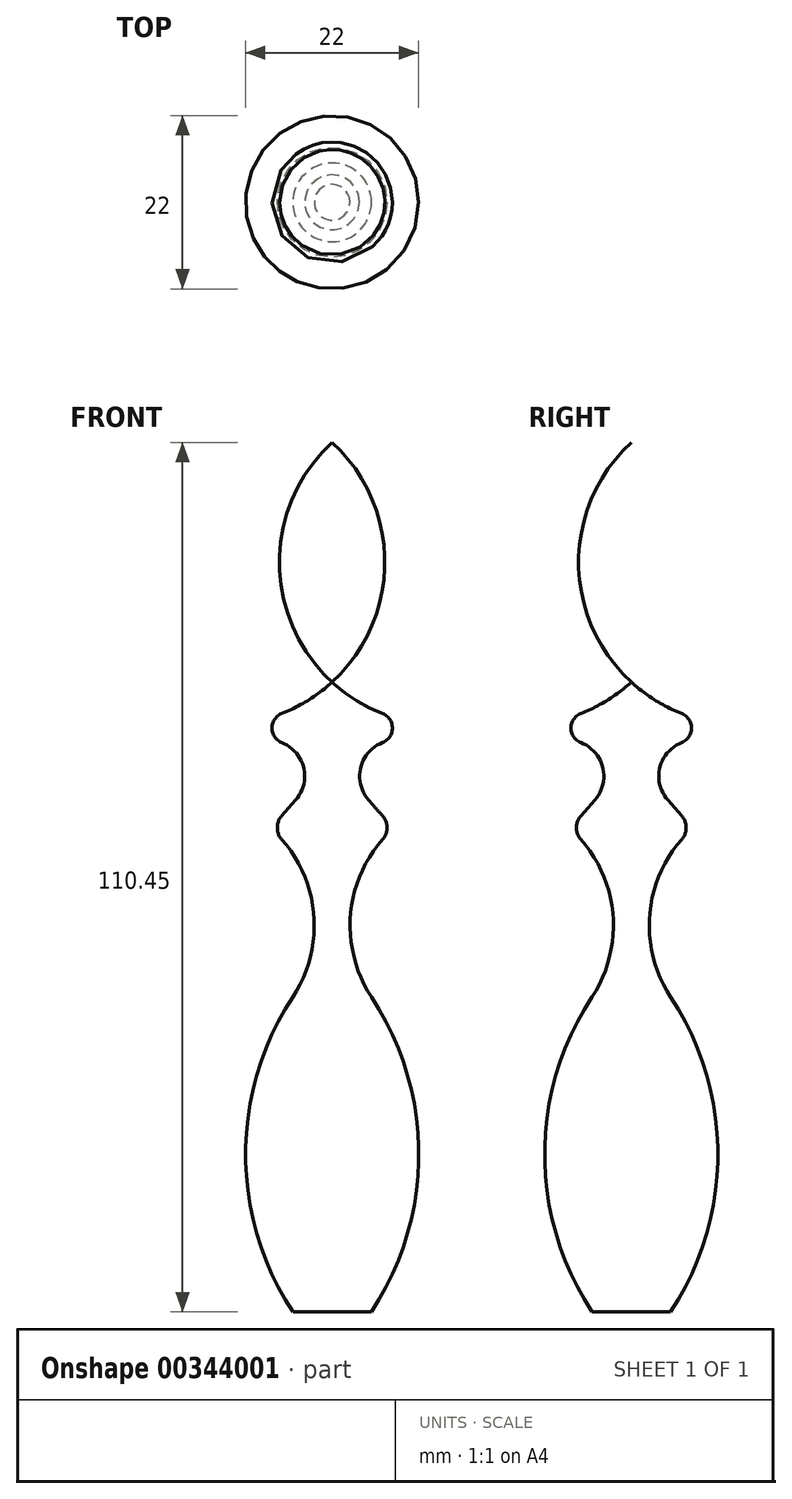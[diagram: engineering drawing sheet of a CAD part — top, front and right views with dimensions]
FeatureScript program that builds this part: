
annotation { "Feature Type Name" : "Feature", "Feature Type Description" : "" }
export const myFeature = defineFeature(function(context is Context, id is Id, definition is map)
    precondition{}
    {
        {
            var Q0;
            Q0=qCreatedBy(makeId("Front.planeOp"),FACE);
            var sketch = newSketch(context, id + "F0", { "sketchPlane" : qUnion([Q0])});
            skArc(sketch, "E0", {"start": v(5, -80) * mm, "mid": v(11, -60) * mm, "end": v(5, -40) * mm});
            skLineSegment(sketch, "E1", {"start": v(5, -80) * mm, "end": v(0, -80) * mm});
            skLineSegment(sketch, "E2", {"start": v(0, -80) * mm, "end": v(0, 0) * mm});
            skArc(sketch, "E3", {"start": v(6.4, -20) * mm, "mid": v(6.97, -18.5) * mm, "end": v(6.4, -17) * mm});
            skLineSegment(sketch, "E4", {"start": v(6.4, -17) * mm, "end": v(4.64, -15) * mm});
            skArc(sketch, "E5", {"start": v(6.4, -7.68) * mm, "mid": v(3.62, -10.88) * mm, "end": v(4.64, -15) * mm});
            skArc(sketch, "E6", {"start": v(6.4, -7.68) * mm, "mid": v(7.66, -5.84) * mm, "end": v(6.4, -4) * mm});
            skArc(sketch, "E7", {"start": v(0, 0) * mm, "mid": v(3.02, -2.3) * mm, "end": v(6.4, -4) * mm});
            skArc(sketch, "E8", {"start": v(6.4, -20) * mm, "mid": v(2.32, -29.76) * mm, "end": v(5, -40) * mm});
            skSolve(sketch);
        }
        {
            var Q0;
            Q0=sQuery(id+"F0.wireOp",EDGE,"E1");
            var Q1;
            Q1=sQuery(id+"F0.wireOp",EDGE,"E8");
            var Q2;
            Q2=sQuery(id+"F0.wireOp",EDGE,"E3");
            var Q3;
            Q3=sQuery(id+"F0.wireOp",EDGE,"E4");
            var Q4;
            Q4=sQuery(id+"F0.wireOp",EDGE,"E5");
            var Q5;
            Q5=sQuery(id+"F0.wireOp",EDGE,"E6");
            var Q6;
            Q6=sQuery(id+"F0.wireOp",EDGE,"E7");
            var Q7;
            Q7=sQuery(id+"F0.wireOp",EDGE,"E0");
            var Q8;
            Q8=sQuery(id+"F0.wireOp",EDGE,"E2");
            revolve(context, id + "F1", {"bodyType" : ToolBodyType.SURFACE, "surfaceEntities" : qUnion([Q0, Q1, Q2, Q3, Q4, Q5, Q6, Q7]), "axis" : qUnion([Q8]), "revolveType" : RevolveType.FULL});
        }
    });
